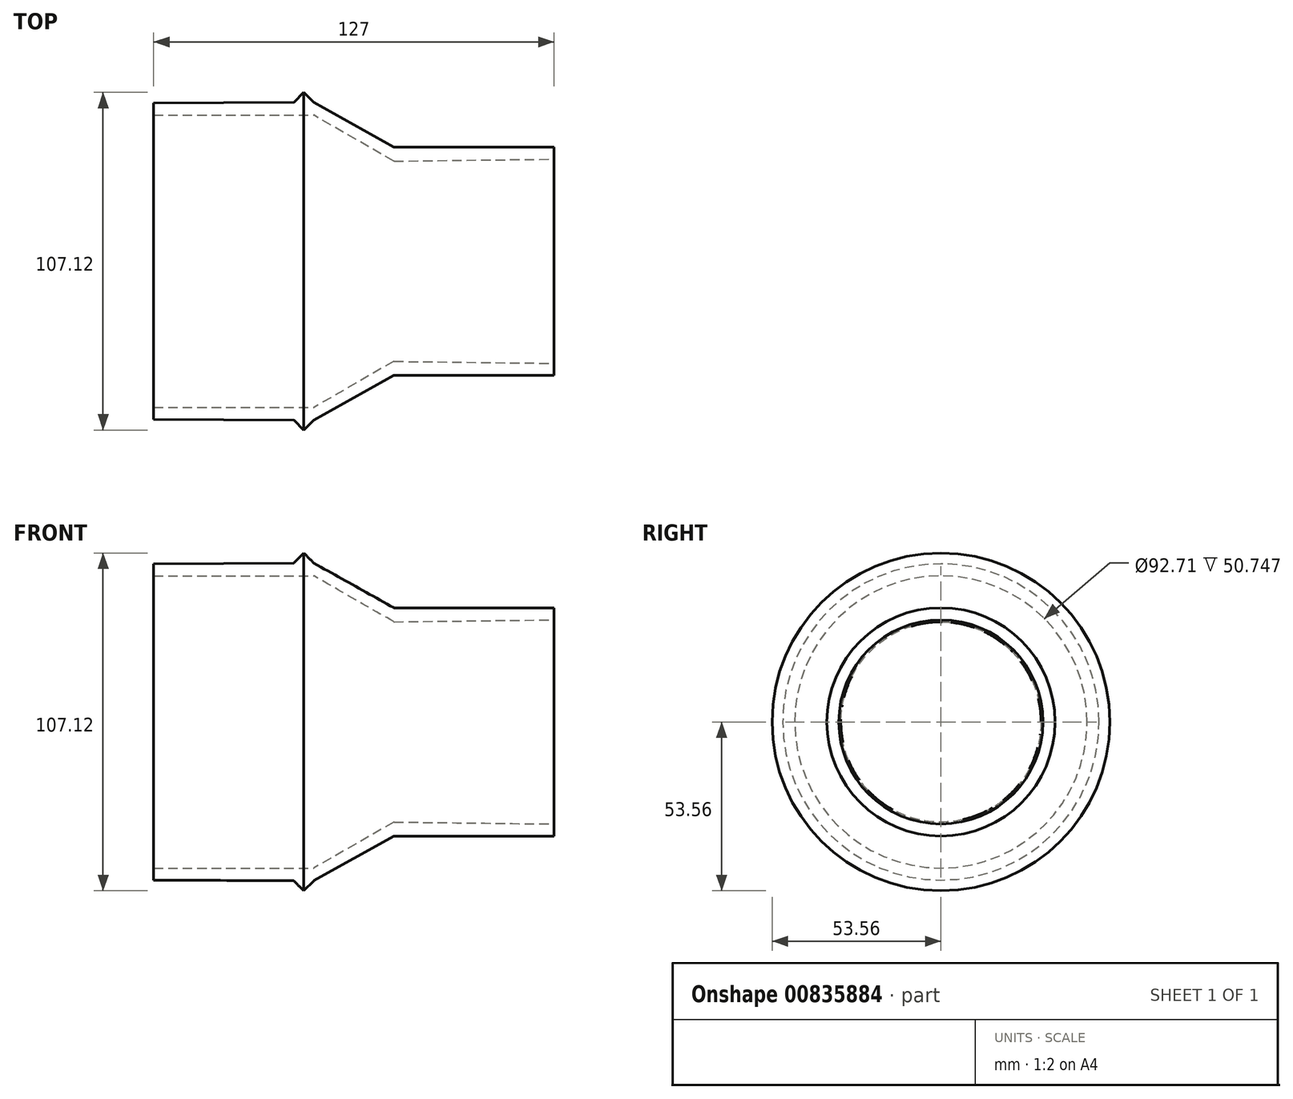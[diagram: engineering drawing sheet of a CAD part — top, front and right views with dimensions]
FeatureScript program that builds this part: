
annotation { "Feature Type Name" : "Feature", "Feature Type Description" : "" }
export const myFeature = defineFeature(function(context is Context, id is Id, definition is map)
    precondition{}
    {
        {
            assignVariable(context, id + "F0", {"name" : "fillet", "anyValue" : .2});
        }
        {
            var Q0;
            Q0=qCreatedBy(makeId("Front.planeOp"),FACE);
            var sketch = newSketch(context, id + "F1", { "sketchPlane" : qUnion([Q0])});
            skLineSegment(sketch, "E0", {"start": v(0, 0) * mm, "end": v(-48.8, 0) * mm, "construction": true});
            skLineSegment(sketch, "E1", {"start": v(0, 31.75) * mm, "end": v(50.8, 32.39) * mm});
            skLineSegment(sketch, "E2", {"start": v(50.8, 32.39) * mm, "end": v(50.8, 36.2) * mm});
            skLineSegment(sketch, "E3", {"start": v(50.8, 36.2) * mm, "end": v(0, 36.2) * mm});
            skPoint(sketch, "E4", {"position": v(0, 31.75) * mm});
            skLineSegment(sketch, "E5", {"start": v(0, 36.2) * mm, "end": v(-25.4, 50.39) * mm});
            skLineSegment(sketch, "E6", {"start": v(-25.4, 50.39) * mm, "end": v(-28.57, 53.56) * mm});
            skLineSegment(sketch, "E7", {"start": v(-28.58, 53.56) * mm, "end": v(-31.75, 50.39) * mm});
            skLineSegment(sketch, "E8", {"start": v(-31.75, 50.39) * mm, "end": v(-76.2, 50.16) * mm});
            skLineSegment(sketch, "E9", {"start": v(-76.2, 50.16) * mm, "end": v(-76.2, 46.35) * mm});
            skLineSegment(sketch, "E10", {"start": v(-76.2, 46.35) * mm, "end": v(-25.4, 46.36) * mm});
            skLineSegment(sketch, "E11", {"start": v(-25.4, 46.36) * mm, "end": v(0, 31.75) * mm});
            skLineSegment(sketch, "E12", {"start": v(-31.75, 50.39) * mm, "end": v(-25.4, 50.39) * mm, "construction": true});
            skLineSegment(sketch, "E13", {"start": v(-25.4, 50.39) * mm, "end": v(-25.4, 46.36) * mm, "construction": true});
            skLineSegment(sketch, "E14", {"start": v(-28.58, 50.39) * mm, "end": v(-28.58, 53.56) * mm, "construction": true});
            skPoint(sketch, "E15", {"position": v(-50.8, 50.3) * mm});
            skSolve(sketch);
        }
        {
            var Q0;
            Q0 = qSketchRegion(id + "F1", true);
            var Q1;
            Q1=sQuery(id+"F1.wireOp",EDGE,"E0");
            revolve(context, id + "F2", {"surfaceOperationType" : NewSurfaceOperationType.NEW, "entities" : qUnion([Q0]), "axis" : qUnion([Q1]), "revolveType" : RevolveType.FULL});
        }
        {
            var Q0;
            Q0=makeQuery(id+"F2.opRevolve","SWEPT_EDGE",EDGE,{"disambiguationData":[OSD([sQuery(id+"F1.wireOp",EDGE,"E10"),sQuery(id+"F1.wireOp",EDGE,"E11")])]});
            var Q1;
            Q1=makeQuery(id+"F2.opRevolve","SWEPT_EDGE",EDGE,{"disambiguationData":[OSD([sQuery(id+"F1.wireOp",EDGE,"E1"),sQuery(id+"F1.wireOp",EDGE,"E11")])]});
            var Q2;
            Q2=makeQuery(id+"F2.opRevolve","SWEPT_EDGE",EDGE,{"disambiguationData":[OSD([sQuery(id+"F1.wireOp",EDGE,"E3"),sQuery(id+"F1.wireOp",EDGE,"E5")])]});
            var Q3;
            Q3=makeQuery(id+"F2.opRevolve","SWEPT_EDGE",EDGE,{"disambiguationData":[OSD([sQuery(id+"F1.wireOp",EDGE,"E7"),sQuery(id+"F1.wireOp",EDGE,"E8")])]});
            var Q4;
            Q4=makeQuery(id+"F2.opRevolve","SWEPT_EDGE",EDGE,{"disambiguationData":[OSD([sQuery(id+"F1.wireOp",EDGE,"E5"),sQuery(id+"F1.wireOp",EDGE,"E6")])]});
            fillet(context, id + "F3", {"entities" : qUnion([Q0, Q1, Q2, Q3, Q4]), "radius" : (getVariable(context, 'fillet')) * mm, "tangentPropagation" : true, "allowEdgeOverflow" : false});
        }
    });
